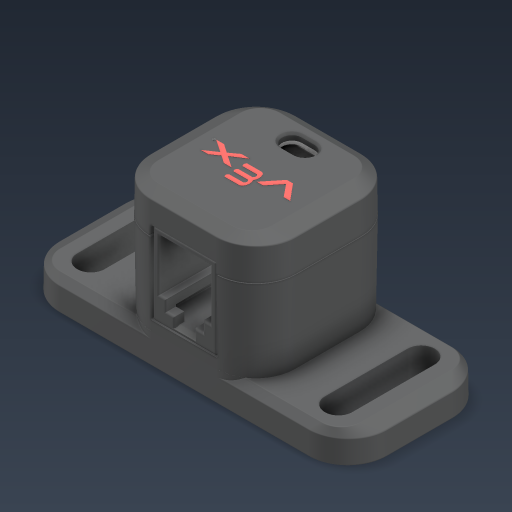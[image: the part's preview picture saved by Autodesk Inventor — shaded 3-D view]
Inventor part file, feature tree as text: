
AUTODESK INVENTOR PART (.ipt)
format: ipt  version: 2023 (Build 270158000, 158)  size: 1,990,656 bytes
history: native  units: in
note: dims shown in document units (in); Inventor stores cm internally (conversion verified against a paired STEP export)
features: other x12, extrude x3, sketch x3
ambient origin geometry x8: Origin, YZ Plane, XZ Plane, XY Plane, X Axis, Y Axis, Z Axis, Center Point
bodies: Solid1 (feature_tree), Solid2 (feature_tree), Solid3 (feature_tree), Solid4 (feature_tree), Solid5 (feature_tree), Solid6 (feature_tree), Solid7 (feature_tree), Solid8 (feature_tree), Solid9 (feature_tree), Solid10 (feature_tree)
feature tree (18):
  other  "V5 Distance Sensor.iam"
  other  "276-7043-001 Web_Dual Flange.ipt:1"
  other  "276-7043-002 Web.ipt:1"
  other  "276-4852-003 Web.ipt:1"
  other  "228-2677-006 Web.ipt:1"
  other  "228-2677-006 Web.ipt:2"
  other  "228-2677-006 Web.ipt:3"
  other  "228-2677-006 Web.ipt:4"
  other  "276-4852-006 Web.ipt:1"
  other  "276-4852-900 Web.iam:1::Part15^276-4852-900 Web.ipt:1"
  extrude  "Extrusion1"  Depth=0.3937in
  sketch  "Sketch1"  dims[d0=0.3937in d1=0.089in]
  other  "Srf1"
  sketch  "Sketch2"  dims[d2=1.0in d3=0.0in d4=0.089in]
  other  "Srf2"
  sketch  "Sketch3"  dims[d5=1.0in d6=0.0in d18=0.002in d19=0.0in]
  extrude  "ExtrusionSrf1"  Depth=0.089in
  extrude  "ExtrusionSrf2"  Depth=0.002in TaperAngle=0.0deg
